# Revit family: ROTHOB_Rothoblaas_Screw_HBSPlateA4
name_source: partatom
category: Structural Connections
units: mm (PartAtom-declared; Revit-internal decimal feet)

## family parameters
Cut with Voids When Loaded = No
Enable cutting in views = Yes
Host = Face
Material for Model Behavior = Steel
OmniClass Number = 23.20.40.11.14.24
OmniClass Title = Screws
Shared = No

## types (18) — shared parameters
AssetType = Fixed
BIMObjectName = ROTHOB_Rothoblaas_Screw_HBSPlateA4
CECode = ETA-11/0030
CETitle = Rotho Blaas Self-tapping screws and threaded rods
Category = Pr_20_29_76_75: Self-tapping screws
CodePerformance = CE - Construction products
Color = Silver
Default Elevation = 1219.2 mm
Description = Pan head screws for plates
DurationUnit = Years
Esporta tipo in formato IFC con nome = IfcMechanicalFastenerType
ExpectedLife = 50
Features = Self-tapping screws for steel-timber connections
Finish = Stainless steel
HeadType = Reinforced pan head
ICC-ESCode = ESR-4645
ICC-ESTitle = Rotho blaas self-tapping wood screws
IfcExportAs = IfcMechanicalFastenerType
IfcExportType = USERDEFINED
ManufacturerName = ROTHO BLAAS SRL
ManufacturerURL = www.rothoblaas.com
Material = A4 | AISI316 austenitic stainless steel (CRC III)
ModelDisclaimer = The latest version of the data sheets can be found on our website
Name = Screw
ObjectMaterial = ROTHOB_Rothoblaas_StainlessSteelAISI316
OmniClassCode = 23.20.40.11.14.24
OmniClassTitle = Screws
OmniClassVersion = 2012-05-16
ProductInformation = www.rothoblaas.com/products/fastening/screws/hbs-plate-a4
Revision = 000
Shape = Cylindrical
Tipo IFC predefinito = USERDEFINED
UniClass2015Code = Pr_20_29_76_75
UniClass2015Title = Self-tapping screws
UniClass2015Version = Products v1.38
Version = 001

## per-type parameters (varying)
| type | BitType | GTIN | H1 | H2 | HeadDiameter_dk | HeadThickness_t1 | InsertionLength_L | ModelNumber | ModelNumberCode | NominalDiameter | NominalDiameter_d1 | NominalLength | ShankDiameter_ds | ShankLength | Size | ThreadDiameter_d2 | ThreadLength_b | ThreadRadius | TipLength | UnderheadDiameter | UnderheadLength | WasherThickness_tk |
| HBSPL860A4_8x60mm | 40 | 8059386077207 | 3.0032 mm  [stored 0.00985302 ft] | 1.1571 mm  [stored 0.00379626 ft] | 13.5 mm  [stored 0.0442913 ft] | 6.6 mm  [stored 0.0216535 ft] | 60 mm | HBSPL860A4 | 860 | 8 mm  [stored 0.0262467 ft] | 8 mm  [stored 0.0262467 ft] | 60 mm | 6.3 mm  [stored 0.0206693 ft] | 1.4183 mm  [stored 0.00465321 ft] | 8x60 mm | 5.9 mm  [stored 0.019357 ft] | 52 mm | 2.95 mm  [stored 0.00967848 ft] | 11.8318 mm  [stored 0.0388182 ft] | 10 mm  [stored 0.0328084 ft] | 3 mm  [stored 0.00984252 ft] | 4 mm  [stored 0.0131234 ft] |
| HBSPL880A4_8x80mm | 40 | 8059386077252 | 3.0032 mm  [stored 0.00985302 ft] | 1.1571 mm  [stored 0.00379626 ft] | 13.5 mm  [stored 0.0442913 ft] | 6.6 mm  [stored 0.0216535 ft] | 80 mm | HBSPL880A4 | 880 | 8 mm  [stored 0.0262467 ft] | 8 mm  [stored 0.0262467 ft] | 80 mm | 6.3 mm  [stored 0.0206693 ft] | 18.4183 mm  [stored 0.0604275 ft] | 8x80 mm | 5.9 mm  [stored 0.019357 ft] | 55 mm | 2.95 mm  [stored 0.00967848 ft] | 11.8318 mm  [stored 0.0388182 ft] | 10 mm  [stored 0.0328084 ft] | 3 mm  [stored 0.00984252 ft] | 4 mm  [stored 0.0131234 ft] |
| HBSPL8100A4_8x100mm | 40 | 8059386077238 | 3.0032 mm  [stored 0.00985302 ft] | 1.1571 mm  [stored 0.00379626 ft] | 13.5 mm  [stored 0.0442913 ft] | 6.6 mm  [stored 0.0216535 ft] | 100 mm | HBSPL8100A4 | 8100 | 8 mm  [stored 0.0262467 ft] | 8 mm  [stored 0.0262467 ft] | 100 mm | 6.3 mm  [stored 0.0206693 ft] | 18.4183 mm  [stored 0.0604275 ft] | 8x100 mm | 5.9 mm  [stored 0.019357 ft] | 75 mm | 2.95 mm  [stored 0.00967848 ft] | 11.8318 mm  [stored 0.0388182 ft] | 10 mm  [stored 0.0328084 ft] | 3 mm  [stored 0.00984252 ft] | 4 mm  [stored 0.0131234 ft] |
| HBSPL8120A4_8x120mm | 40 | 8059386077245 | 3.0032 mm  [stored 0.00985302 ft] | 1.1571 mm  [stored 0.00379626 ft] | 13.5 mm  [stored 0.0442913 ft] | 6.6 mm  [stored 0.0216535 ft] | 120 mm | HBSPL8120A4 | 8120 | 8 mm  [stored 0.0262467 ft] | 8 mm  [stored 0.0262467 ft] | 120 mm | 6.3 mm  [stored 0.0206693 ft] | 18.4183 mm  [stored 0.0604275 ft] | 8x120 mm | 5.9 mm  [stored 0.019357 ft] | 95 mm | 2.95 mm  [stored 0.00967848 ft] | 11.8318 mm  [stored 0.0388182 ft] | 10 mm  [stored 0.0328084 ft] | 3 mm  [stored 0.00984252 ft] | 4 mm  [stored 0.0131234 ft] |
| HBSPL8140A4_8x140mm | 40 | 8059386077269 | 3.0032 mm  [stored 0.00985302 ft] | 1.1571 mm  [stored 0.00379626 ft] | 13.5 mm  [stored 0.0442913 ft] | 6.6 mm  [stored 0.0216535 ft] | 140 mm | HBSPL8140A4 | 8140 | 8 mm  [stored 0.0262467 ft] | 8 mm  [stored 0.0262467 ft] | 140 mm | 6.3 mm  [stored 0.0206693 ft] | 23.4183 mm | 8x140 mm | 5.9 mm  [stored 0.019357 ft] | 110 mm | 2.95 mm  [stored 0.00967848 ft] | 11.8318 mm  [stored 0.0388182 ft] | 10 mm  [stored 0.0328084 ft] | 3 mm  [stored 0.00984252 ft] | 4 mm  [stored 0.0131234 ft] |
| HBSPL8160A4_8x160mm | 40 | 8059386077160 | 3.0032 mm  [stored 0.00985302 ft] | 1.1571 mm  [stored 0.00379626 ft] | 13.5 mm  [stored 0.0442913 ft] | 6.6 mm  [stored 0.0216535 ft] | 160 mm | HBSPL8160A4 | 8160 | 8 mm  [stored 0.0262467 ft] | 8 mm  [stored 0.0262467 ft] | 160 mm | 6.3 mm  [stored 0.0206693 ft] | 23.4183 mm | 8x160 mm | 5.9 mm  [stored 0.019357 ft] | 130 mm | 2.95 mm  [stored 0.00967848 ft] | 11.8318 mm  [stored 0.0388182 ft] | 10 mm  [stored 0.0328084 ft] | 3 mm  [stored 0.00984252 ft] | 4 mm  [stored 0.0131234 ft] |
| HBSPL1080A4_10x80mm | 40 | 8059386077214 | 3.5556 mm  [stored 0.0116654 ft] | 0.835 mm  [stored 0.0027395 ft] | 16.5 mm  [stored 0.0541339 ft] | 7.6 mm | 80 mm | HBSPL1080A4 | 1080 | 10 mm  [stored 0.0328084 ft] | 10 mm  [stored 0.0328084 ft] | 80 mm | 7.2 mm  [stored 0.023622 ft] | 12.5547 mm  [stored 0.04119 ft] | 10x80 mm | 6.6 mm  [stored 0.0216535 ft] | 60 mm | 3.3 mm  [stored 0.0108268 ft] | 13.2356 mm  [stored 0.0434239 ft] | 12 mm  [stored 0.0393701 ft] | 3.4722 mm  [stored 0.0113917 ft] | 4.5 mm  [stored 0.0147638 ft] |
| HBSPL10100A4_10x100mm | 40 | 8059386077054 | 3.5556 mm  [stored 0.0116654 ft] | 0.835 mm  [stored 0.0027395 ft] | 16.5 mm  [stored 0.0541339 ft] | 7.6 mm | 100 mm | HBSPL10100A4 | 10100 | 10 mm  [stored 0.0328084 ft] | 10 mm  [stored 0.0328084 ft] | 100 mm | 7.2 mm  [stored 0.023622 ft] | 17.5547 mm  [stored 0.0575942 ft] | 10x100 mm | 6.6 mm  [stored 0.0216535 ft] | 75 mm | 3.3 mm  [stored 0.0108268 ft] | 13.2356 mm  [stored 0.0434239 ft] | 12 mm  [stored 0.0393701 ft] | 3.4722 mm  [stored 0.0113917 ft] | 4.5 mm  [stored 0.0147638 ft] |
| HBSPL10120A4_10x120mm | 40 | 8059386076842 | 3.5556 mm  [stored 0.0116654 ft] | 0.835 mm  [stored 0.0027395 ft] | 16.5 mm  [stored 0.0541339 ft] | 7.6 mm | 120 mm | HBSPL10120A4 | 10120 | 10 mm  [stored 0.0328084 ft] | 10 mm  [stored 0.0328084 ft] | 120 mm | 7.2 mm  [stored 0.023622 ft] | 17.5547 mm  [stored 0.0575942 ft] | 10x120 mm | 6.6 mm  [stored 0.0216535 ft] | 95 mm | 3.3 mm  [stored 0.0108268 ft] | 13.2356 mm  [stored 0.0434239 ft] | 12 mm  [stored 0.0393701 ft] | 3.4722 mm  [stored 0.0113917 ft] | 4.5 mm  [stored 0.0147638 ft] |
| HBSPL10140A4_10x140mm | 40 | 8059386076897 | 3.5556 mm  [stored 0.0116654 ft] | 0.835 mm  [stored 0.0027395 ft] | 16.5 mm  [stored 0.0541339 ft] | 7.6 mm | 140 mm | HBSPL10140A4 | 10140 | 10 mm  [stored 0.0328084 ft] | 10 mm  [stored 0.0328084 ft] | 140 mm | 7.2 mm  [stored 0.023622 ft] | 22.5547 mm  [stored 0.0739984 ft] | 10x140 mm | 6.6 mm  [stored 0.0216535 ft] | 110 mm | 3.3 mm  [stored 0.0108268 ft] | 13.2356 mm  [stored 0.0434239 ft] | 12 mm  [stored 0.0393701 ft] | 3.4722 mm  [stored 0.0113917 ft] | 4.5 mm  [stored 0.0147638 ft] |
| HBSPL10160A4_10x160mm | 40 | 8059386077221 | 3.5556 mm  [stored 0.0116654 ft] | 0.835 mm  [stored 0.0027395 ft] | 16.5 mm  [stored 0.0541339 ft] | 7.6 mm | 160 mm | HBSPL10160A4 | 10160 | 10 mm  [stored 0.0328084 ft] | 10 mm  [stored 0.0328084 ft] | 160 mm | 7.2 mm  [stored 0.023622 ft] | 22.5547 mm  [stored 0.0739984 ft] | 10x160 mm | 6.6 mm  [stored 0.0216535 ft] | 130 mm | 3.3 mm  [stored 0.0108268 ft] | 13.2356 mm  [stored 0.0434239 ft] | 12 mm  [stored 0.0393701 ft] | 3.4722 mm  [stored 0.0113917 ft] | 4.5 mm  [stored 0.0147638 ft] |
| HBSPL10180A4_10x180mm | 40 | 8059386076927 | 3.5556 mm  [stored 0.0116654 ft] | 0.835 mm  [stored 0.0027395 ft] | 16.5 mm  [stored 0.0541339 ft] | 7.6 mm | 180 mm | HBSPL10180A4 | 10180 | 10 mm  [stored 0.0328084 ft] | 10 mm  [stored 0.0328084 ft] | 180 mm | 7.2 mm  [stored 0.023622 ft] | 22.5547 mm  [stored 0.0739984 ft] | 10x180 mm | 6.6 mm  [stored 0.0216535 ft] | 150 mm | 3.3 mm  [stored 0.0108268 ft] | 13.2356 mm  [stored 0.0434239 ft] | 12 mm  [stored 0.0393701 ft] | 3.4722 mm  [stored 0.0113917 ft] | 4.5 mm  [stored 0.0147638 ft] |
| HBSPL12100A4_12x100mm | 50 | 8059386077023 | 4.0332 mm | 1.7279 mm  [stored 0.00566896 ft] | 18.5 mm  [stored 0.0606955 ft] | 8.5 mm | 100 mm | HBSPL12100A4 | 12100 | 12 mm  [stored 0.0393701 ft] | 12 mm  [stored 0.0393701 ft] | 100 mm | 8.55 mm  [stored 0.0280512 ft] | 16.1256 mm  [stored 0.0529055 ft] | 12x100 mm | 7.3 mm  [stored 0.0239501 ft] | 75 mm | 3.65 mm  [stored 0.0119751 ft] | 14.6393 mm | 13 mm | 3.9834 mm  [stored 0.0130689 ft] | 5 mm  [stored 0.0164042 ft] |
| HBSPL12120A4_12x120mm | 50 | 8059386077030 | 4.0332 mm | 1.7279 mm  [stored 0.00566896 ft] | 18.5 mm  [stored 0.0606955 ft] | 8.5 mm | 120 mm | HBSPL12120A4 | 12120 | 12 mm  [stored 0.0393701 ft] | 12 mm  [stored 0.0393701 ft] | 120 mm | 8.55 mm  [stored 0.0280512 ft] | 21.1194 mm  [stored 0.0692894 ft] | 12x120 mm | 7.3 mm  [stored 0.0239501 ft] | 90 mm | 3.65 mm  [stored 0.0119751 ft] | 14.6393 mm | 13 mm | 3.9834 mm  [stored 0.0130689 ft] | 5 mm  [stored 0.0164042 ft] |
| HBSPL12140A4_12x140mm | 50 | 8059386076996 | 4.0332 mm | 1.7279 mm  [stored 0.00566896 ft] | 18.5 mm  [stored 0.0606955 ft] | 8.5 mm | 140 mm | HBSPL12140A4 | 12140 | 12 mm  [stored 0.0393701 ft] | 12 mm  [stored 0.0393701 ft] | 140 mm | 8.55 mm  [stored 0.0280512 ft] | 21.1194 mm  [stored 0.0692894 ft] | 12x140 mm | 7.3 mm  [stored 0.0239501 ft] | 110 mm | 3.65 mm  [stored 0.0119751 ft] | 14.6393 mm | 13 mm | 3.9834 mm  [stored 0.0130689 ft] | 5 mm  [stored 0.0164042 ft] |
| HBSPL12160A4_12x160mm | 50 | 8059386077177 | 4.0332 mm | 1.7279 mm  [stored 0.00566896 ft] | 18.5 mm  [stored 0.0606955 ft] | 8.5 mm | 160 mm | HBSPL12160A4 | 12160 | 12 mm  [stored 0.0393701 ft] | 12 mm  [stored 0.0393701 ft] | 160 mm | 8.55 mm  [stored 0.0280512 ft] | 31.1194 mm | 12x160 mm | 7.3 mm  [stored 0.0239501 ft] | 120 mm | 3.65 mm  [stored 0.0119751 ft] | 14.6393 mm | 13 mm | 3.9834 mm  [stored 0.0130689 ft] | 5 mm  [stored 0.0164042 ft] |
| HBSPL12180A4_12x180mm | 50 | 8059386077047 | 4.0332 mm | 1.7279 mm  [stored 0.00566896 ft] | 18.5 mm  [stored 0.0606955 ft] | 8.5 mm | 180 mm | HBSPL12180A4 | 12180 | 12 mm  [stored 0.0393701 ft] | 12 mm  [stored 0.0393701 ft] | 180 mm | 8.55 mm  [stored 0.0280512 ft] | 31.1194 mm | 12x180 mm | 7.3 mm  [stored 0.0239501 ft] | 140 mm | 3.65 mm  [stored 0.0119751 ft] | 14.6393 mm | 13 mm | 3.9834 mm  [stored 0.0130689 ft] | 5 mm  [stored 0.0164042 ft] |
| HBSPL12200A4_12x200mm | 50 | 8059386077009 | 4.0332 mm | 1.7279 mm  [stored 0.00566896 ft] | 18.5 mm  [stored 0.0606955 ft] | 8.5 mm | 200 mm | HBSPL12200A4 | 12200 | 12 mm  [stored 0.0393701 ft] | 12 mm  [stored 0.0393701 ft] | 200 mm | 8.55 mm  [stored 0.0280512 ft] | 31.1194 mm | 12x200 mm | 7.3 mm  [stored 0.0239501 ft] | 160 mm | 3.65 mm  [stored 0.0119751 ft] | 14.6393 mm | 13 mm | 3.9834 mm  [stored 0.0130689 ft] | 5 mm  [stored 0.0164042 ft] |

note: [stored X ft] marks values corroborated as IEEE doubles in the binary element streams (Revit-internal decimal feet)
